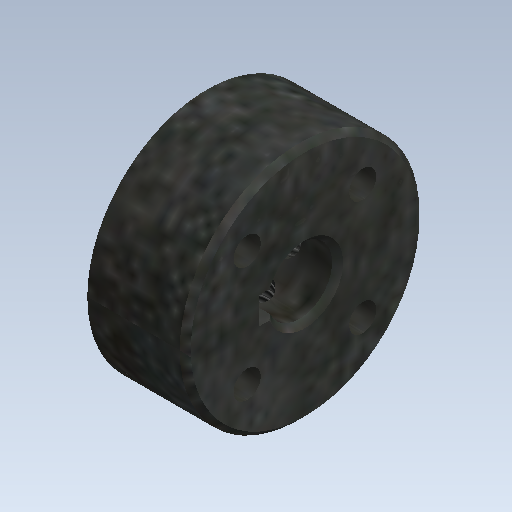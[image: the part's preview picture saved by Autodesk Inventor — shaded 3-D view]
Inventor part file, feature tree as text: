
AUTODESK INVENTOR PART (.ipt)
format: ipt  version: 2021 (Build 250183000, 183)  size: 265,216 bytes
history: native  units: mm (DEFAULTED — no unit token found)
features: other x9, sketch x8, extrude x5, revolve x3, thread x2, direct_edit x2
ambient origin geometry x8: Origin, YZ Plane, XZ Plane, XY Plane, X Axis, Y Axis, Z Axis, Center Point
bodies: Solid1 (feature_tree)
feature tree (29):
  revolve  "Revolution1"  Angle=360.0deg
  revolve  "Revolution2"  Angle=360.0deg
  thread  "Thread1"  [1 undecoded]
  revolve  "Revolution3"  [1 undecoded]
  thread  "Thread2"  [1 undecoded]
  extrude  "Extrusion1"  Depth=10.0mm TaperAngle=0.0deg
  extrude  "Extrusion2"  Depth=1.0mm
  extrude  "Extrusion3"  [1 undecoded]
  extrude  "Extrusion4"  [1 undecoded]
  extrude  "Extrusion5"  [1 undecoded]
  other  "part_XY"
  other  "part_YZ"
  other  "part_ZX"
  other  "part_X"
  other  "part_Y"
  other  "part_Z"
  other  "part_Center"
  direct_edit  "Direct Edit1"
  direct_edit  "Direct Edit3"
  sketch  "Sketch_1"  dims[d0=360.0deg d1=360.0deg]
  sketch  "Sketch_4"  dims[d13=10.0mm d14=0.0mm d15=10.0mm d16=0.0mm]
  sketch  "Sketch_3"  dims[d7=10.0mm d8=0.0mm d9=10.0mm d10=0.0mm d11=10.0mm d12=0.0mm]
  sketch  "Sketch_2"  dims[d2=7.621mm d3=0.0mm d4=360.0deg d5=7.621mm d6=0.0mm]
  sketch  "Sketch_6"  dims[d17=0.0mm d18=1.0mm]
  sketch  "Sketch_7"  dims[d20=-1.0mm]
  sketch  "Sketch_8"
  sketch  "Sketch_9"
  other  "Size1"
  other  "Size3"
note: 6 required parameter values undecoded (feature->parameter linkage not recoverable at this tier; creation-order binding heuristic only, values carry confidence <= 0.55)